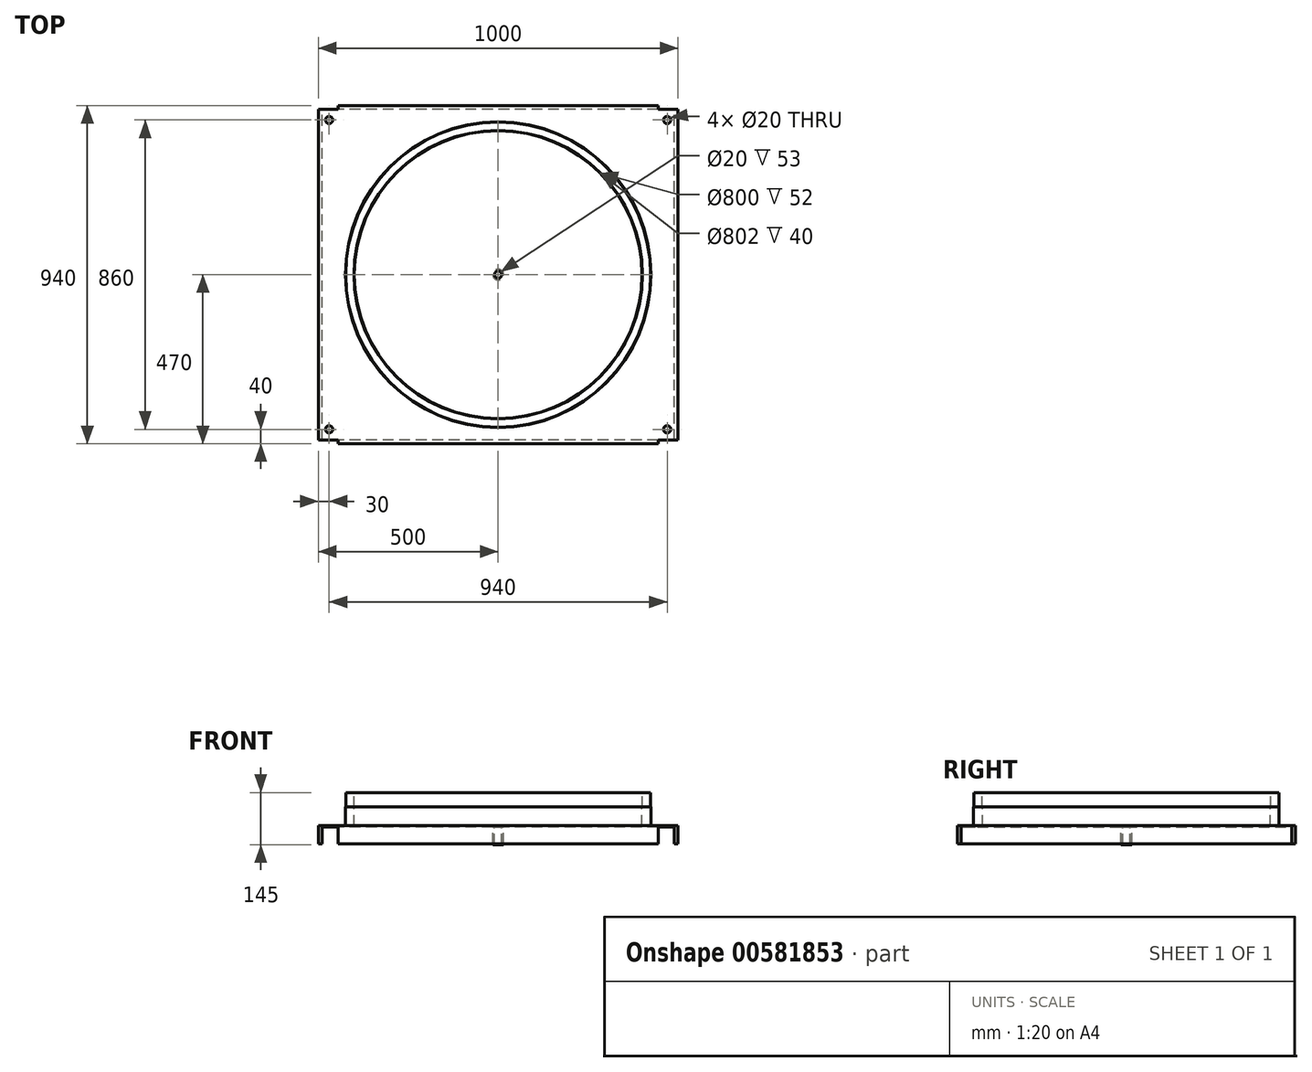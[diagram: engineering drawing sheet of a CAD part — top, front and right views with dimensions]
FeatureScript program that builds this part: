
annotation { "Feature Type Name" : "Feature", "Feature Type Description" : "" }
export const myFeature = defineFeature(function(context is Context, id is Id, definition is map)
    precondition{}
    {
        {
            var Q0;
            Q0=qCreatedBy(makeId("Front.planeOp"),FACE);
            var sketch = newSketch(context, id + "F0", { "sketchPlane" : qUnion([Q0])});
            skLineSegment(sketch, "E0", {"start": v(0, 74.87) * mm, "end": v(0, -73.71) * mm, "construction": true});
            skLineSegment(sketch, "E1", {"start": v(0, 374.84) * mm, "end": v(0, 1) * mm, "construction": true});
            skLineSegment(sketch, "E2", {"start": v(-400, 3) * mm, "end": v(-400, 55) * mm});
            skLineSegment(sketch, "E3", {"start": v(-400, 55) * mm, "end": v(-401, 55) * mm});
            skLineSegment(sketch, "E4", {"start": v(-401, 55) * mm, "end": v(-401, 95) * mm});
            skLineSegment(sketch, "E5", {"start": v(-401, 95) * mm, "end": v(-424, 95) * mm});
            skLineSegment(sketch, "E6", {"start": v(-424, 95) * mm, "end": v(-424, 55) * mm});
            skLineSegment(sketch, "E7", {"start": v(-424, 55) * mm, "end": v(-425, 55) * mm});
            skLineSegment(sketch, "E8", {"start": v(-425, 55) * mm, "end": v(-425, 3) * mm});
            skLineSegment(sketch, "E9", {"start": v(-425, 3) * mm, "end": v(-400, 3) * mm});
            skLineSegment(sketch, "E10.trimOffspring", {"start": v(0, 0) * mm, "end": v(0, -528.94) * mm, "construction": true});
            skLineSegment(sketch, "E11.bottom", {"start": v(-425, 3) * mm, "end": v(-10, 3) * mm});
            skLineSegment(sketch, "E11.top", {"start": v(-425, 0) * mm, "end": v(-10, 0) * mm});
            skLineSegment(sketch, "E11.left", {"start": v(-425, 3) * mm, "end": v(-425, 0) * mm});
            skLineSegment(sketch, "E11.right", {"start": v(-10, 3) * mm, "end": v(-10, 0) * mm});
            skSolve(sketch);
        }
        {
            var Q0;
            Q0=qSketchRegion(id+"F0",true);
            var Q1;
            Q1=sQuery(id+"F0.wireOp",EDGE,"E1");
            revolve(context, id + "F1", {"entities" : qUnion([Q0]), "axis" : qUnion([Q1]), "revolveType" : RevolveType.FULL});
        }
        {
            var Q0;
            Q0=qCreatedBy(makeId("Top.planeOp"),FACE);
            var sketch = newSketch(context, id + "F2", { "sketchPlane" : qUnion([Q0])});
            skLineSegment(sketch, "E12.bottom", {"start": v(500, 460) * mm, "end": v(-500, 460) * mm});
            skLineSegment(sketch, "E12.top", {"start": v(500, -460) * mm, "end": v(-500, -460) * mm});
            skLineSegment(sketch, "E12.left", {"start": v(500, 460) * mm, "end": v(500, -460) * mm});
            skLineSegment(sketch, "E12.right", {"start": v(-500, 460) * mm, "end": v(-500, -460) * mm});
            skPoint(sketch, "E12.middle", {"position": v(0, 0) * mm});
            skCircle(sketch, "E13.0", {"center": v(0, 0) * mm, "radius": 401 * mm});
            skCircle(sketch, "E14.0", {"center": v(0, 0) * mm, "radius": 400 * mm});
            skCircle(sketch, "E15", {"center": v(0, 0) * mm, "radius": 300 * mm});
            skLineSegment(sketch, "E16", {"start": v(0, 0) * mm, "end": v(0, 773.78) * mm, "construction": true});
            skLineSegment(sketch, "E17", {"start": v(0, 0) * mm, "end": v(1007.48, 0) * mm, "construction": true});
            skCircle(sketch, "E18", {"center": v(470, 430) * mm, "radius": 10 * mm});
            skCircle(sketch, "E19.MirrorC", {"center": v(-470, 430) * mm, "radius": 10 * mm});
            skCircle(sketch, "E20.MirrorC", {"center": v(470, -430) * mm, "radius": 10 * mm});
            skCircle(sketch, "E21.MirrorC", {"center": v(-470, -430) * mm, "radius": 10 * mm});
            skSolve(sketch);
        }
        {
            var Q0;
            Q0=qSketchRegion(id+"F2",true);
            extrude(context, id + "F3", {"entities" : qUnion([Q0]), "operationType" : NewBodyOperationType.ADD, "depth" : 3 * mm, "offsetDistance" : 25 * mm});
        }
        {
            var Q0;
            Q0=makeQuery(id+"F3.opExtrude","CAP_FACE",FACE,{"disambiguationData":[OSD([sQuery(id+"F2.wireOp",EDGE,"E12.bottom"),sQuery(id+"F2.wireOp",EDGE,"E12.top"),sQuery(id+"F2.wireOp",EDGE,"E12.left"),sQuery(id+"F2.wireOp",EDGE,"E12.right"),sQuery(id+"F2.wireOp",EDGE,"E15"),sQuery(id+"F2.wireOp",EDGE,"E18"),sQuery(id+"F2.wireOp",EDGE,"E19.MirrorC"),sQuery(id+"F2.wireOp",EDGE,"E20.MirrorC"),sQuery(id+"F2.wireOp",EDGE,"E21.MirrorC")])],"isStart":false});
            var sketch = newSketch(context, id + "F4", { "sketchPlane" : qUnion([Q0])});
            skLineSegment(sketch, "E22", {"start": v(0, 0) * mm, "end": v(-1098.02, 0) * mm, "construction": true});
            skLineSegment(sketch, "E23", {"start": v(0, 0) * mm, "end": v(0, -1084.2) * mm, "construction": true});
            skLineSegment(sketch, "E24.bottom", {"start": v(445, -460) * mm, "end": v(-445, -460) * mm});
            skLineSegment(sketch, "E24.top", {"start": v(445, -470) * mm, "end": v(-445, -470) * mm});
            skLineSegment(sketch, "E24.left", {"start": v(445, -460) * mm, "end": v(445, -470) * mm});
            skLineSegment(sketch, "E24.right", {"start": v(-445, -460) * mm, "end": v(-445, -470) * mm});
            skLineSegment(sketch, "E25.bottom", {"start": v(-500, -460) * mm, "end": v(-490, -460) * mm});
            skLineSegment(sketch, "E25.top", {"start": v(-500, 460) * mm, "end": v(-490, 460) * mm});
            skLineSegment(sketch, "E25.left", {"start": v(-500, 460) * mm, "end": v(-500, -460) * mm});
            skLineSegment(sketch, "E25.right", {"start": v(-490, 460) * mm, "end": v(-490, -460) * mm});
            skLineSegment(sketch, "E26.MirrorCS", {"start": v(445, 460) * mm, "end": v(445, 470) * mm});
            skLineSegment(sketch, "E27.MirrorCS", {"start": v(-445, 460) * mm, "end": v(-445, 470) * mm});
            skLineSegment(sketch, "E28.MirrorCS", {"start": v(445, 470) * mm, "end": v(-445, 470) * mm});
            skLineSegment(sketch, "E29.MirrorCS", {"start": v(445, 460) * mm, "end": v(-445, 460) * mm});
            skLineSegment(sketch, "E30.MirrorCS", {"start": v(500, 460) * mm, "end": v(490, 460) * mm});
            skLineSegment(sketch, "E31.MirrorCS", {"start": v(500, -460) * mm, "end": v(490, -460) * mm});
            skLineSegment(sketch, "E32.MirrorCS", {"start": v(500, 460) * mm, "end": v(500, -460) * mm});
            skLineSegment(sketch, "E33.MirrorCS", {"start": v(490, 460) * mm, "end": v(490, -460) * mm});
            skLineSegment(sketch, "E34.MirrorCS", {"start": v(0, 0) * mm, "end": v(1098.02, 0) * mm, "construction": true});
            skSolve(sketch);
        }
        {
            var Q0;
            Q0=qSketchRegion(id+"F4",true);
            extrude(context, id + "F5", {"entities" : qUnion([Q0]), "operationType" : NewBodyOperationType.ADD, "oppositeDirection" : true, "depth" : 50 * mm, "offsetDistance" : 25 * mm});
        }
        {
            var Q0;
            Q0=makeQuery(id+"F3.boolean.opBoolean","MERGE",FACE,{"derivedFrom":[makeQuery(id+"F1.opRevolve","SWEPT_FACE",FACE,{"disambiguationData":[OSD([sQuery(id+"F0.wireOp",EDGE,"E11.top")])]}),makeQuery(id+"F3.opExtrude","CAP_FACE",FACE,{"disambiguationData":[OSD([sQuery(id+"F2.wireOp",EDGE,"E12.bottom"),sQuery(id+"F2.wireOp",EDGE,"E12.top"),sQuery(id+"F2.wireOp",EDGE,"E12.left"),sQuery(id+"F2.wireOp",EDGE,"E12.right"),sQuery(id+"F2.wireOp",EDGE,"E13.0"),sQuery(id+"F2.wireOp",EDGE,"E18"),sQuery(id+"F2.wireOp",EDGE,"E19.MirrorC"),sQuery(id+"F2.wireOp",EDGE,"E20.MirrorC"),sQuery(id+"F2.wireOp",EDGE,"E21.MirrorC")])],"isStart":false})]});
            var sketch = newSketch(context, id + "F6", { "sketchPlane" : qUnion([Q0])});
            skCircle(sketch, "E35.0", {"center": v(0, 0) * mm, "radius": 10 * mm});
            skCircle(sketch, "E36", {"center": v(0, 0) * mm, "radius": 15 * mm});
            skSolve(sketch);
        }
        {
            var Q0;
            Q0=qSketchRegion(id+"F6",true);
            extrude(context, id + "F7", {"entities" : qUnion([Q0]), "operationType" : NewBodyOperationType.ADD, "depth" : 50 * mm, "offsetDistance" : 25 * mm});
        }
    });
